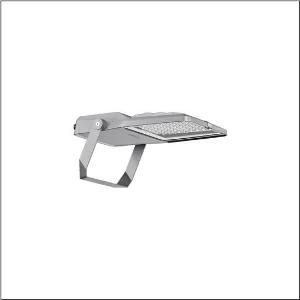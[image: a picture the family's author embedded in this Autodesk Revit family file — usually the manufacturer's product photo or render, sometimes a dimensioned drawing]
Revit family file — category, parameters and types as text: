
# Revit family: floodlight_fl_21_iq_mini___pl33t_5xa7771c2f1a_64ec
name_source: partatom
category: Lighting Fixtures
units: mm (PartAtom-declared; Revit-internal decimal feet)

## family parameters
Cut with Voids When Loaded = No
Host = Face
Light Source = No
Part Type = Normal
Room Calculation Point = No
Round Connector Dimension = Use Diameter
Shared = No

## types (1)
- --- (1 x LED, 12060 lm, 87.2 W, 3000K)
    Apparent Load = 87 VA
    CIE Flux Codes = 26 75 99 100 100
    Color Rendering = 70
    Color Temperature = 3000K
    Default Elevation = 1800 mm
    Description = Floodlight FL 21 iQ mini, floodlight, primary light control with lens, of PMMA, primary optical cover: protective disc, of toughened safety glass, transparent, light distribution: PL33T, light emission: direct distribution, installation type: surface-mounted, LED, High Power LED, rated luminous flux: 12.060lm, luminous efficacy: 138lm/W, light colour: 730, colour temperature: 3000K, control: Auto-Match, Temp-Guard, Lumen-Switch, Night-Set, Smart-Wire, Light-Fading, Desk-Remote (wireless, voltage-free reading and setting of iQ features in the workshop via application-optimized NFC function/RFID function), optimised constant luminous flux control (CLO 2.0), with terminal, 6-pole, mains connection: 220..240V, AC, 50/60Hz, start of lifetime: 87W, end of service life: 92W, reduction: 40W, luminaire housing, of diecast aluminium, powder-coated, Siteco® metallic grey (DB 702S), corrosivity category C5 mid according to DIN EN ISO 12944, sealing non-destructively replaceable, mounting bracket, of steel, galvanised, powder-coated, Siteco® metallic grey (DB 702S), protection rating (complete): IP66, insulation class (complete): insulation class II (safety insulation), certification: CE, ENEC, VDE, protection symbol: D, impact resistance: IK08, permissible operating ambient temperature: -40..+40°C, permissible operating ambient temperature for outdoor applications: -40..+50°C, standard: DIN EN 12944, LABS conformity tested according to VDMA 24364:2018-05, packaging unit: 1 piece

Light Distribution: PL33T
    Height = 70 mm
    Lamp = 1 x LED
    Lamp Light Flux = 12060 lm
    Lamp Power = 87.2 W
    Lamp count = 1
    Length = 485 mm
    Luminous efficacy = 138 lm/W
    Manufacturer = Siteco
    ModVariant = No
    Model = 5XA7771C2F1A
    Number of Poles = 1
    OnlyDefault = Yes
    Power Factor = 1
    Product Name = Floodlight FL 21 iQ mini | PL33T
    Product group = floodlight | pylon annexe
    ProductGroupID = 6200
    Protection Class = Protection class II
    Protection Degree = IP 66
    RLX_Detail_Level = 1
    RLX_Emergency_Light_Flux = 0 lm
    RLX_Emergency_Type = 0
    RLX_Emergency_Type_DB = No
    RlxData = <blob elided: 96189 chars, md5=4412e670>
    Socket = socket
    Standby Power = 0 W
    System Light Flux = 12060 lm
    System Power = 87 W
    Type Comments = factory setting: luminous flux: 100 % | dim-lin: 254 | 456 mA
    Type Image = l_1006845.jpg
    URL = http://relux.com
    VarID = @adj_082299
    Voltage = 0 V
    Weight = 0.00 kg
    Width = 337 mm

## geometry (parser evidence)
native form markers: Blend x4, Sweep x11
no freeform markers — native parametric forms only
